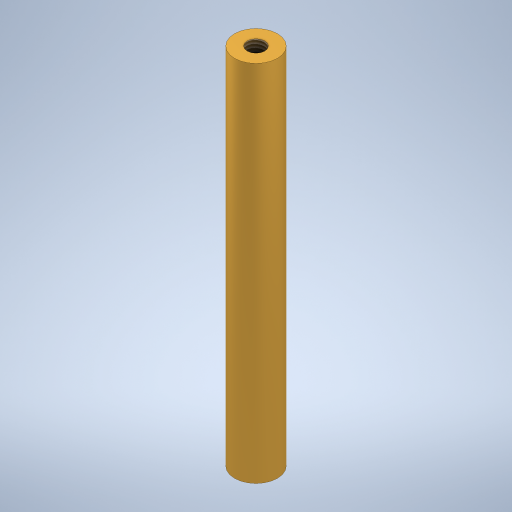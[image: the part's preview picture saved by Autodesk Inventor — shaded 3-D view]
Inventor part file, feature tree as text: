
AUTODESK INVENTOR PART (.ipt)
format: ipt  version: 2023 (Build 270158000, 158)  size: 255,488 bytes
history: native  units: mm
features: sketch x3, hole x2, other x1, extrude x1
ambient origin geometry x8: Origin, YZ Plane, XZ Plane, XY Plane, X Axis, Y Axis, Z Axis, Center Point
bodies: Body1 (feature_tree)
feature tree (7):
  other  "Sólido1"
  extrude  "Extrusão1"  Depth=85.0mm TaperAngle=0.0deg
  hole  "Furo1"  [1 undecoded]
  hole  "Furo2"  [1 undecoded]
  sketch  "Esboço1"  dims[d1=10.0mm d2=85.0mm d3=0.0mm]
  sketch  "Esboço2"  dims[d4=4.134mm d5=10.0mm d6=4.0mm d7=2.0mm d8=90.0deg d9=14.2mm d10=20.594885mm]
  sketch  "Esboço3"  dims[d11=4.134mm d12=10.0mm d13=4.0mm d14=2.0mm d15=90.0deg d16=14.2mm d17=20.594885mm]
note: 2 required parameter values undecoded (feature->parameter linkage not recoverable at this tier; creation-order binding heuristic only, values carry confidence <= 0.55)
